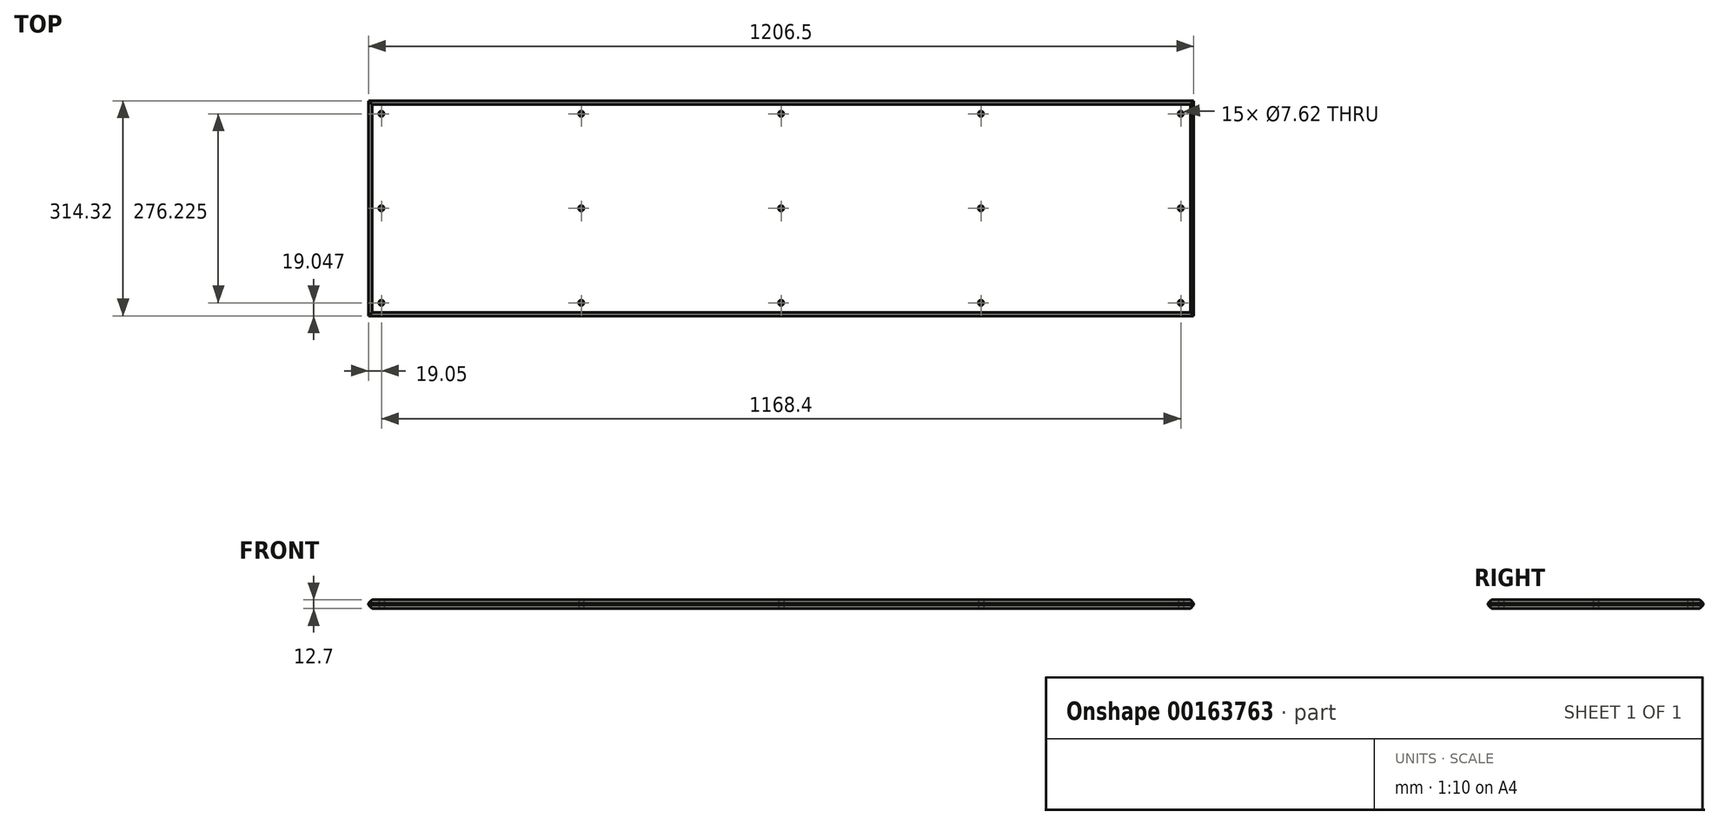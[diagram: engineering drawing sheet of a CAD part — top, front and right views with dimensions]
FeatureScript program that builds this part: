
annotation { "Feature Type Name" : "Feature", "Feature Type Description" : "" }
export const myFeature = defineFeature(function(context is Context, id is Id, definition is map)
    precondition{}
    {
        {
            var Q0;
            Q0=qCreatedBy(makeId("Top.planeOp"),FACE);
            var sketch = newSketch(context, id + "F0", { "sketchPlane" : qUnion([Q0])});
            skLineSegment(sketch, "E0.bottom", {"start": v(603.25, 157.16) * mm, "end": v(-603.25, 157.16) * mm});
            skLineSegment(sketch, "E0.top", {"start": v(603.25, -157.16) * mm, "end": v(-603.25, -157.16) * mm});
            skLineSegment(sketch, "E0.left", {"start": v(603.25, 157.16) * mm, "end": v(603.25, -157.16) * mm});
            skLineSegment(sketch, "E0.right", {"start": v(-603.25, 157.16) * mm, "end": v(-603.25, -157.16) * mm});
            skPoint(sketch, "E0.middle", {"position": v(0, 0) * mm});
            skLineSegment(sketch, "E1.bottom", {"start": v(-603.25, 157.16) * mm, "end": v(-584.2, 157.16) * mm});
            skLineSegment(sketch, "E1.top", {"start": v(-603.25, 138.11) * mm, "end": v(-584.2, 138.11) * mm});
            skLineSegment(sketch, "E1.left", {"start": v(-603.25, 157.16) * mm, "end": v(-603.25, 138.11) * mm});
            skLineSegment(sketch, "E1.right", {"start": v(-584.2, 157.16) * mm, "end": v(-584.2, 138.11) * mm});
            skCircle(sketch, "E2", {"center": v(-584.2, 138.11) * mm, "radius": 3.81 * mm});
            skCircle(sketch, "E3.0.1.0", {"center": v(-584.2, 0) * mm, "radius": 3.81 * mm});
            skCircle(sketch, "E3.0.2.0", {"center": v(-584.2, -138.11) * mm, "radius": 3.81 * mm});
            skCircle(sketch, "E3.1.0.0", {"center": v(-292.1, 138.11) * mm, "radius": 3.81 * mm});
            skCircle(sketch, "E3.1.1.0", {"center": v(-292.1, 0) * mm, "radius": 3.81 * mm});
            skCircle(sketch, "E3.1.2.0", {"center": v(-292.1, -138.11) * mm, "radius": 3.81 * mm});
            skCircle(sketch, "E3.2.0.0", {"center": v(0, 138.11) * mm, "radius": 3.81 * mm});
            skCircle(sketch, "E3.2.1.0", {"center": v(0, 0) * mm, "radius": 3.81 * mm});
            skCircle(sketch, "E3.2.2.0", {"center": v(0, -138.11) * mm, "radius": 3.81 * mm});
            skCircle(sketch, "E3.3.0.0", {"center": v(292.1, 138.11) * mm, "radius": 3.81 * mm});
            skCircle(sketch, "E3.3.1.0", {"center": v(292.1, 0) * mm, "radius": 3.81 * mm});
            skCircle(sketch, "E3.3.2.0", {"center": v(292.1, -138.11) * mm, "radius": 3.81 * mm});
            skCircle(sketch, "E3.4.0.0", {"center": v(584.2, 138.11) * mm, "radius": 3.81 * mm});
            skCircle(sketch, "E3.4.1.0", {"center": v(584.2, 0) * mm, "radius": 3.81 * mm});
            skCircle(sketch, "E3.4.2.0", {"center": v(584.2, -138.11) * mm, "radius": 3.81 * mm});
            skLineSegment(sketch, "E3.direction1", {"start": v(-584.2, 138.11) * mm, "end": v(-292.1, 138.11) * mm, "construction": true});
            skLineSegment(sketch, "E3.direction2", {"start": v(-584.2, 138.11) * mm, "end": v(-584.2, 0) * mm, "construction": true});
            skSolve(sketch);
        }
        {
            var Q0;
            Q0 = qSketchRegion(id + "F0", true);
            extrude(context, id + "F1", {"entities" : qUnion([Q0]), "depth" : 12.7 * mm, "offsetDistance" : 25.4 * mm});
        }
        {
            var Q0;
            Q0=makeQuery(id+"F1.opExtrude","CAP_EDGE",EDGE,{"disambiguationData":[OSD([sQuery(id+"F0.wireOp",EDGE,"E0.bottom"),sQuery(id+"F0.wireOp",EDGE,"E1.bottom")])],"isStart":true});
            var Q1;
            Q1=makeQuery(id+"F1.opExtrude","CAP_EDGE",EDGE,{"disambiguationData":[OSD([sQuery(id+"F0.wireOp",EDGE,"E0.left")])],"isStart":true});
            var Q2;
            Q2=makeQuery(id+"F1.opExtrude","CAP_EDGE",EDGE,{"disambiguationData":[OSD([sQuery(id+"F0.wireOp",EDGE,"E0.top")])],"isStart":true});
            var Q3;
            Q3=makeQuery(id+"F1.opExtrude","CAP_EDGE",EDGE,{"disambiguationData":[OSD([sQuery(id+"F0.wireOp",EDGE,"E0.right"),sQuery(id+"F0.wireOp",EDGE,"E1.left")])],"isStart":true});
            var Q4;
            Q4=makeQuery(id+"F1.opExtrude","CAP_EDGE",EDGE,{"disambiguationData":[OSD([sQuery(id+"F0.wireOp",EDGE,"E0.top")])],"isStart":false});
            var Q5;
            Q5=makeQuery(id+"F1.opExtrude","CAP_EDGE",EDGE,{"disambiguationData":[OSD([sQuery(id+"F0.wireOp",EDGE,"E0.left")])],"isStart":false});
            var Q6;
            Q6=makeQuery(id+"F1.opExtrude","CAP_EDGE",EDGE,{"disambiguationData":[OSD([sQuery(id+"F0.wireOp",EDGE,"E0.bottom"),sQuery(id+"F0.wireOp",EDGE,"E1.bottom")])],"isStart":false});
            var Q7;
            Q7=makeQuery(id+"F1.opExtrude","CAP_EDGE",EDGE,{"disambiguationData":[OSD([sQuery(id+"F0.wireOp",EDGE,"E0.right"),sQuery(id+"F0.wireOp",EDGE,"E1.left")])],"isStart":false});
            chamfer(context, id + "F2", {"entities" : qUnion([Q0, Q1, Q2, Q3, Q4, Q5, Q6, Q7]), "width" : 5.08 * mm, "tangentPropagation" : true});
        }
    });
